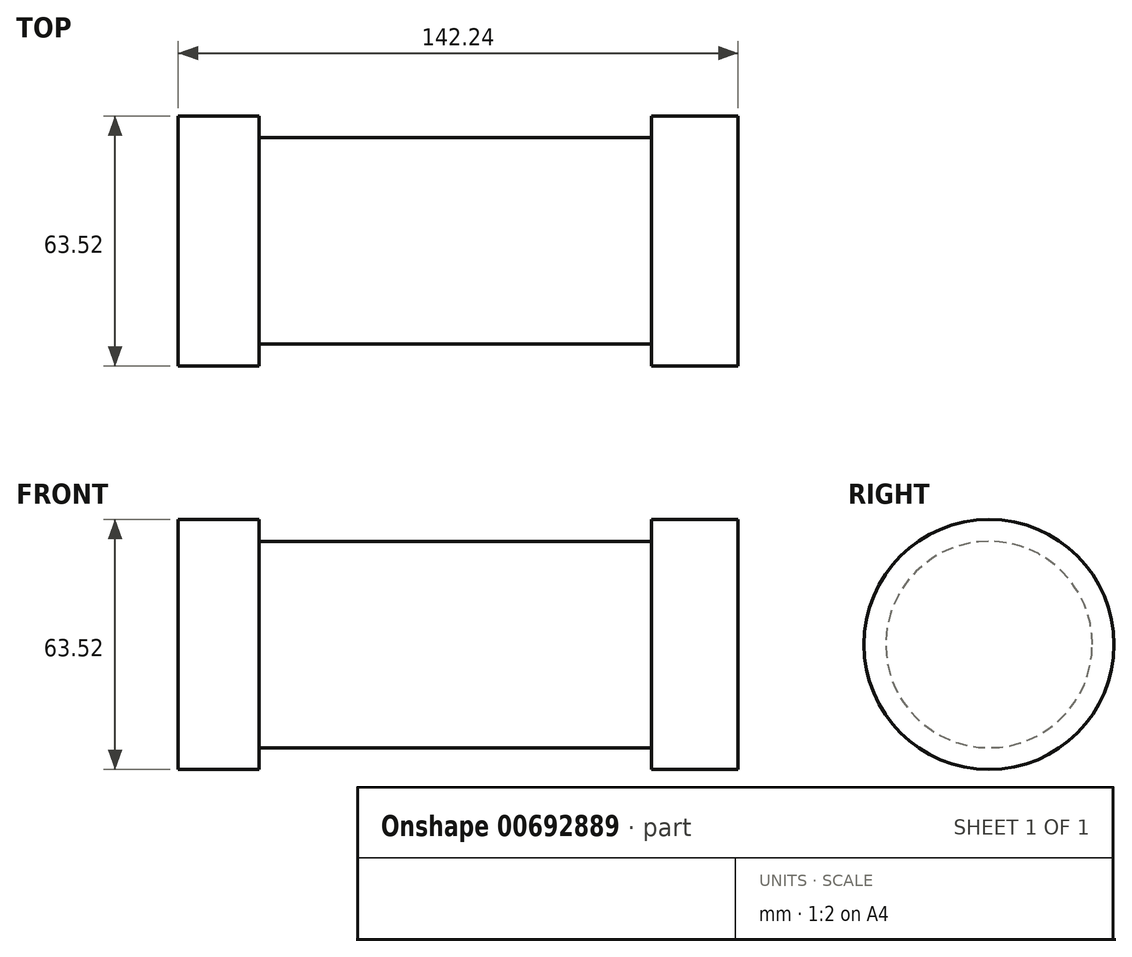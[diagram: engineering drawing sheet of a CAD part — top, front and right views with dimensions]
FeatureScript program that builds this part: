
annotation { "Feature Type Name" : "Feature", "Feature Type Description" : "" }
export const myFeature = defineFeature(function(context is Context, id is Id, definition is map)
    precondition{}
    {
        {
            var Q0;
            Q0=qCreatedBy(makeId("Right.planeOp"),FACE);
            var sketch = newSketch(context, id + "F0", { "sketchPlane" : qUnion([Q0])});
            skCircle(sketch, "E0", {"center": v(0, 0) * mm, "radius": 27.8 * mm});
            skSolve(sketch);
        }
        {
            var Q0;
            Q0 = qSketchRegion(id + "F0", true);
            extrude(context, id + "F1", {"entities" : qUnion([Q0]), "endBound" : BoundingType.SYMMETRIC, "depth" : 111.76 * mm, "offsetDistance" : 25.4 * mm});
        }
        {
            var Q0;
            Q0=qCreatedBy(makeId("Right.planeOp"),FACE);
            var sketch = newSketch(context, id + "F2", { "sketchPlane" : qUnion([Q0])});
            skCircle(sketch, "E1", {"center": v(0, 0) * mm, "radius": 31.76 * mm});
            skSolve(sketch);
        }
        {
            var Q0;
            Q0 = qSketchRegion(id + "F2", true);
            extrude(context, id + "F3", {"entities" : qUnion([Q0]), "operationType" : NewBodyOperationType.ADD, "endBound" : BoundingType.SYMMETRIC, "depth" : 142.24 * mm, "offsetDistance" : 25.4 * mm});
        }
        {
            var Q0;
            Q0=qCreatedBy(makeId("Front.planeOp"),FACE);
            var sketch = newSketch(context, id + "F4", { "sketchPlane" : qUnion([Q0])});
            skLineSegment(sketch, "E2.bottom", {"start": v(-50.56, 32.47) * mm, "end": v(49.15, 32.47) * mm});
            skLineSegment(sketch, "E2.top", {"start": v(-50.56, 26.23) * mm, "end": v(49.15, 26.23) * mm});
            skLineSegment(sketch, "E2.left", {"start": v(-50.56, 32.47) * mm, "end": v(-50.56, 26.23) * mm});
            skLineSegment(sketch, "E2.right", {"start": v(49.15, 32.47) * mm, "end": v(49.15, 26.23) * mm});
            skLineSegment(sketch, "E3", {"start": v(-81.92, 0) * mm, "end": v(79.9, 0) * mm, "construction": true});
            skSolve(sketch);
        }
        {
            var Q0;
            Q0 = qSketchRegion(id + "F4", true);
            var Q1;
            Q1=sQuery(id+"F4.wireOp",EDGE,"E3");
            revolve(context, id + "F5", {"operationType" : NewBodyOperationType.REMOVE, "entities" : qUnion([Q0]), "axis" : qUnion([Q1]), "revolveType" : RevolveType.FULL, "oppositeDirection" : true});
        }
    });
